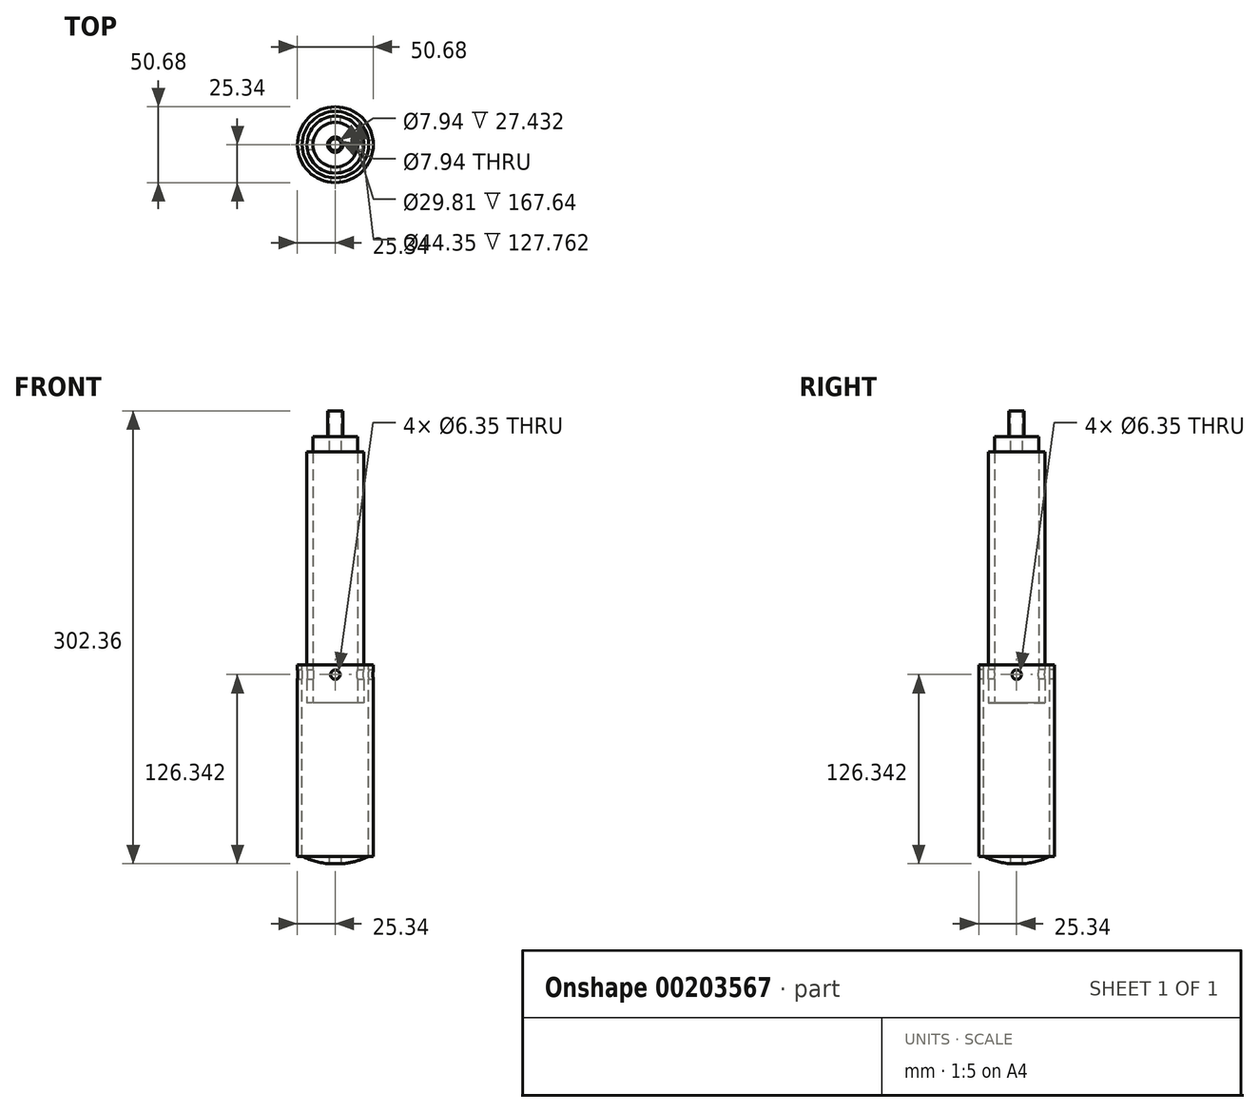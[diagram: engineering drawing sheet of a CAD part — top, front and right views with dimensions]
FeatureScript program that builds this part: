
annotation { "Feature Type Name" : "Feature", "Feature Type Description" : "" }
export const myFeature = defineFeature(function(context is Context, id is Id, definition is map)
    precondition{}
    {
        {
            var Q0;
            Q0=qCreatedBy(makeId("Top.planeOp"),FACE);
            var sketch = newSketch(context, id + "F0", { "sketchPlane" : qUnion([Q0])});
            skCircle(sketch, "E0", {"center": v(0, 0) * mm, "radius": 25.34 * mm});
            skSolve(sketch);
        }
        {
            var Q0;
            Q0 = qSketchRegion(id + "F0", true);
            extrude(context, id + "F1", {"entities" : qUnion([Q0]), "depth" : 127.76 * mm});
        }
        {
            var Q0;
            Q0=makeQuery(id+"F1.opExtrude","CAP_FACE",FACE,{"disambiguationData":[OSD([sQuery(id+"F0.wireOp",EDGE,"E0")])],"isStart":false});
            var sketch = newSketch(context, id + "F2", { "sketchPlane" : qUnion([Q0])});
            skCircle(sketch, "E1", {"center": v(0, 0) * mm, "radius": 22.17 * mm});
            skSolve(sketch);
        }
        {
            var Q0;
            Q0 = qSketchRegion(id + "F2", true);
            extrude(context, id + "F3", {"entities" : qUnion([Q0]), "operationType" : NewBodyOperationType.REMOVE, "endBound" : BoundingType.THROUGH_ALL, "oppositeDirection" : true, "depth" : 159.77 * mm});
        }
        {
            var Q0;
            Q0=makeQuery(id+"F1.opExtrude","CAP_FACE",FACE,{"disambiguationData":[OSD([sQuery(id+"F0.wireOp",EDGE,"E0")])],"isStart":false});
            var sketch = newSketch(context, id + "F4", { "sketchPlane" : qUnion([Q0])});
            skCircle(sketch, "E2", {"center": v(0, 0) * mm, "radius": 19 * mm});
            skCircle(sketch, "E3", {"center": v(0, 0) * mm, "radius": 14.9 * mm});
            skSolve(sketch);
        }
        {
            var Q0;
            Q0 = qSketchRegion(id + "F4", true);
            extrude(context, id + "F5", {"entities" : qUnion([Q0]), "depth" : 142.24 * mm});
        }
        {
            var Q0;
            Q0=makeQuery(id+"F4.imprint","IMPRINT",FACE,{"disambiguationData":[TD([[makeQuery(id+"F4.imprint","IMPRINT",EDGE,{"derivedFrom":sQuery(id+"F4.wireOp",EDGE,"E2")}),1.0]])]});
            extrude(context, id + "F6", {"entities" : qUnion([Q0]), "operationType" : NewBodyOperationType.ADD, "oppositeDirection" : true, "depth" : 25.4 * mm});
        }
        {
            var Q0;
            Q0=qCreatedBy(makeId("Right.planeOp"),FACE);
            var sketch = newSketch(context, id + "F7", { "sketchPlane" : qUnion([Q0])});
            skCircle(sketch, "E4", {"center": v(0, 121.41) * mm, "radius": 3.18 * mm});
            skSolve(sketch);
        }
        {
            var Q0;
            Q0 = qSketchRegion(id + "F7", true);
            extrude(context, id + "F8", {"entities" : qUnion([Q0]), "operationType" : NewBodyOperationType.REMOVE, "endBound" : BoundingType.THROUGH_ALL, "oppositeDirection" : true, "depth" : 25.4 * mm, "hasSecondDirection" : true, "secondDirectionOppositeDirection" : false, "secondDirectionDepth" : 25.4 * mm});
        }
        {
            var Q0;
            Q0=qCreatedBy(makeId("Front.planeOp"),FACE);
            var sketch = newSketch(context, id + "F9", { "sketchPlane" : qUnion([Q0])});
            skCircle(sketch, "E5", {"center": v(0, 121.41) * mm, "radius": 3.18 * mm});
            skSolve(sketch);
        }
        {
            var Q0;
            Q0 = qSketchRegion(id + "F9", true);
            extrude(context, id + "F10", {"entities" : qUnion([Q0]), "operationType" : NewBodyOperationType.REMOVE, "endBound" : BoundingType.THROUGH_ALL, "oppositeDirection" : true, "depth" : 25.4 * mm, "hasSecondDirection" : true, "secondDirectionOppositeDirection" : false, "secondDirectionDepth" : 25.4 * mm});
        }
        {
            var Q0;
            Q0=qCreatedBy(makeId("Right.planeOp"),FACE);
            var sketch = newSketch(context, id + "F11", { "sketchPlane" : qUnion([Q0])});
            skLineSegment(sketch, "E6.0", {"start": v(-22.17, 0) * mm, "end": v(0, 0) * mm});
            skArc(sketch, "E7", {"start": v(-22.17, 0) * mm, "mid": v(-11.37, -3.8) * mm, "end": v(0, -5.08) * mm});
            skLineSegment(sketch, "E8", {"start": v(0, 0) * mm, "end": v(0, -5.08) * mm});
            skPoint(sketch, "E9.orphan", {"position": v(22.17, 0) * mm});
            skSolve(sketch);
        }
        {
            var Q0;
            Q0 = qSketchRegion(id + "F11", true);
            var Q1;
            Q1=sQuery(id+"F11.wireOp",EDGE,"E8");
            revolve(context, id + "F12", {"entities" : qUnion([Q0]), "axis" : qUnion([Q1]), "revolveType" : RevolveType.FULL});
        }
        {
            var Q0;
            Q0=makeQuery(id+"F5.opExtrude","CAP_FACE",FACE,{"disambiguationData":[OSD([sQuery(id+"F4.wireOp",EDGE,"E2"),sQuery(id+"F4.wireOp",EDGE,"E3")])],"isStart":false});
            var sketch = newSketch(context, id + "F13", { "sketchPlane" : qUnion([Q0])});
            skCircle(sketch, "E10.0", {"center": v(0, 0) * mm, "radius": 14.9 * mm});
            skSolve(sketch);
        }
        {
            var Q0;
            Q0 = qSketchRegion(id + "F13", true);
            extrude(context, id + "F14", {"entities" : qUnion([Q0]), "depth" : 10.4 * mm});
        }
        {
            var Q0;
            Q0=makeQuery(id+"F14.opExtrude","CAP_FACE",FACE,{"disambiguationData":[OSD([sQuery(id+"F13.wireOp",EDGE,"E10.0")])],"isStart":false});
            var sketch = newSketch(context, id + "F15", { "sketchPlane" : qUnion([Q0])});
            skCircle(sketch, "E11", {"center": v(0, 0) * mm, "radius": 5.08 * mm});
            skSolve(sketch);
        }
        {
            var Q0;
            Q0 = qSketchRegion(id + "F15", true);
            extrude(context, id + "F16", {"entities" : qUnion([Q0]), "operationType" : NewBodyOperationType.ADD, "depth" : 17.02 * mm});
        }
        {
            var Q0;
            Q0=makeQuery(id+"F16.opExtrude","CAP_FACE",FACE,{"disambiguationData":[OSD([sQuery(id+"F15.wireOp",EDGE,"E11")])],"isStart":false});
            var sketch = newSketch(context, id + "F17", { "sketchPlane" : qUnion([Q0])});
            skCircle(sketch, "E12", {"center": v(0, 0) * mm, "radius": 3.97 * mm});
            skSolve(sketch);
        }
        {
            var Q0;
            Q0 = qSketchRegion(id + "F17", true);
            extrude(context, id + "F18", {"entities" : qUnion([Q0]), "operationType" : NewBodyOperationType.REMOVE, "endBound" : BoundingType.THROUGH_ALL, "oppositeDirection" : true, "depth" : 25.4 * mm});
        }
    });
